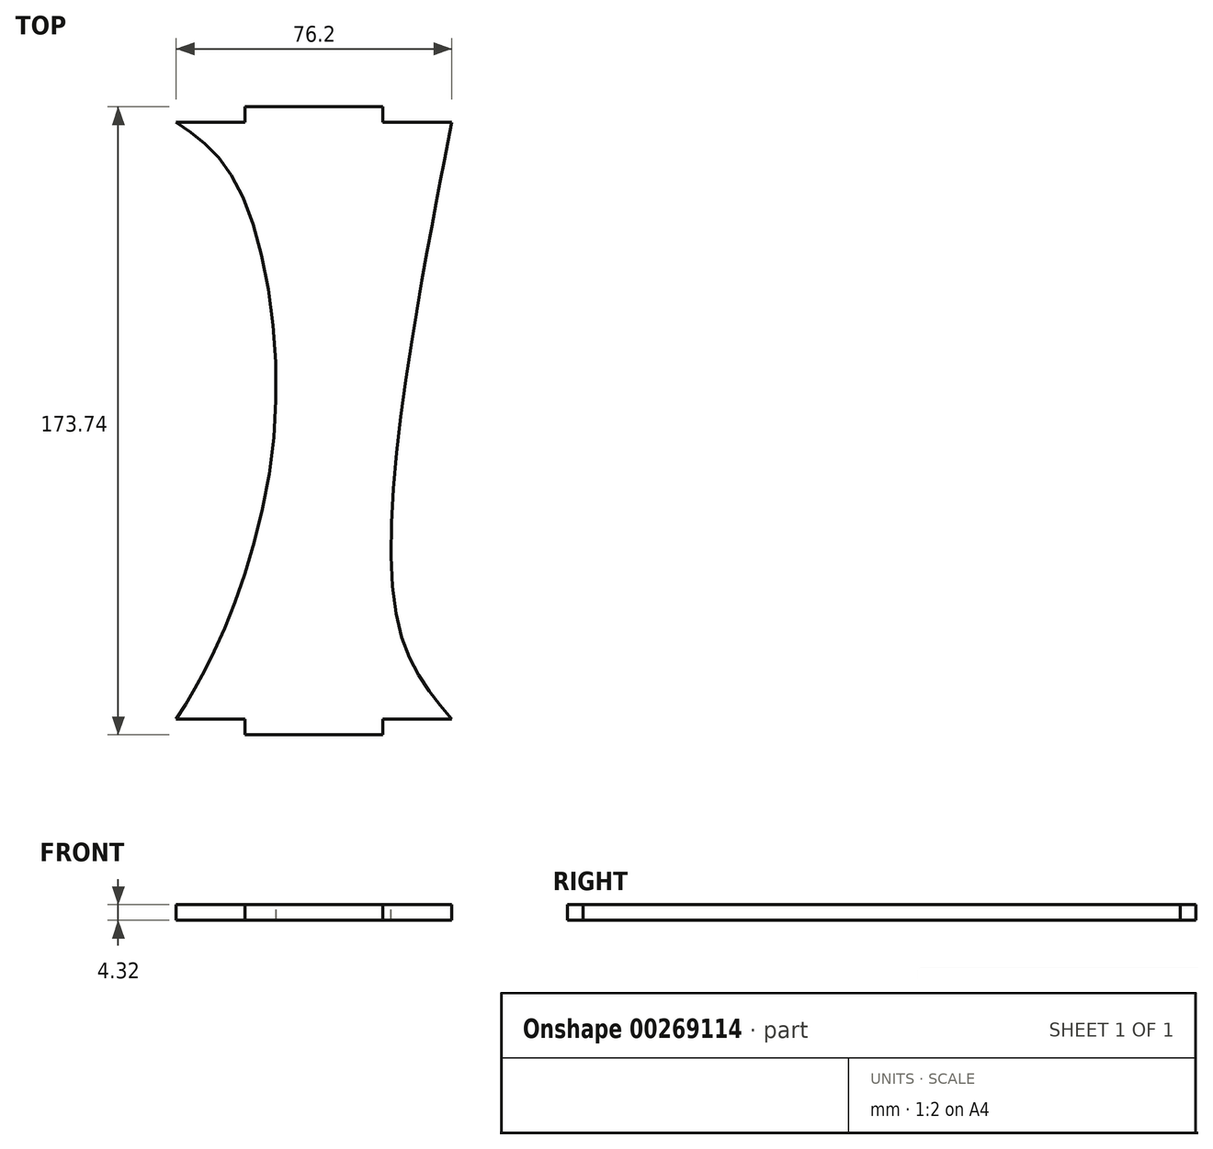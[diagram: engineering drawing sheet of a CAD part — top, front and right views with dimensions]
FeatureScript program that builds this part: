
annotation { "Feature Type Name" : "Feature", "Feature Type Description" : "" }
export const myFeature = defineFeature(function(context is Context, id is Id, definition is map)
    precondition{}
    {
        {
            var Q0;
            Q0=qCreatedBy(makeId("Top.planeOp"),FACE);
            var sketch = newSketch(context, id + "F0", { "sketchPlane" : qUnion([Q0])});
            skLineSegment(sketch, "E0.bottom", {"start": v(0, 0) * mm, "end": v(19.05, 0) * mm});
            skLineSegment(sketch, "E0.top", {"start": v(0, 165.1) * mm, "end": v(19.05, 165.1) * mm});
            skLineSegment(sketch, "E1.top", {"start": v(19.05, 169.42) * mm, "end": v(57.15, 169.42) * mm});
            skLineSegment(sketch, "E1.left", {"start": v(19.05, 165.1) * mm, "end": v(19.05, 169.42) * mm});
            skLineSegment(sketch, "E1.right", {"start": v(57.15, 165.1) * mm, "end": v(57.15, 169.42) * mm});
            skLineSegment(sketch, "E2.top", {"start": v(57.15, -4.32) * mm, "end": v(19.05, -4.32) * mm});
            skLineSegment(sketch, "E2.left", {"start": v(57.15, 0) * mm, "end": v(57.15, -4.32) * mm});
            skLineSegment(sketch, "E2.right", {"start": v(19.05, 0) * mm, "end": v(19.05, -4.32) * mm});
            skLineSegment(sketch, "E3.trimOffspring", {"start": v(57.15, 0) * mm, "end": v(76.2, 0) * mm});
            skLineSegment(sketch, "E4.trimOffspring", {"start": v(57.15, 165.1) * mm, "end": v(76.2, 165.1) * mm});
            skFitSpline(sketch, "E5", {"points": [v(0, 0) * mm, v(11.53, 20.93) * mm, v(27.32, 82.63) * mm, v(15.97, 149.28) * mm, v(0, 165.1) * mm], "startDerivative": vector(59.04, 94.85) * mm, "endDerivative": vector(-92.69, 62.53) * mm});
            skFitSpline(sketch, "E6", {"points": [v(76.2, 165.1) * mm, v(68.06, 122.16) * mm, v(60.71, 29.3) * mm, v(76.2, 0) * mm], "startDerivative": vector(-24.08, -120.6) * mm, "endDerivative": vector(74.27, -87.3) * mm});
            skSolve(sketch);
        }
        {
            var Q0;
            Q0 = qSketchRegion(id + "F0", true);
            extrude(context, id + "F1", {"entities" : qUnion([Q0]), "depth" : 4.32 * mm});
        }
    });
